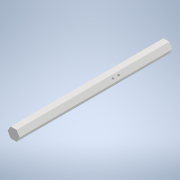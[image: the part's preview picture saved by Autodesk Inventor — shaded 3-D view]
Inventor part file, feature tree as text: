
AUTODESK INVENTOR PART (.ipt)
format: ipt  version: 2022 (Build 260153000, 153)  size: 117,248 bytes
history: native  units: mm
features: other x4, reference x3, extrude x2, sketch x2
ambient origin geometry x8: Origin, YZ Plane, XZ Plane, XY Plane, X Axis, Y Axis, Z Axis, Center Point
bodies: Solid1 (feature_tree)
feature tree (11):
  extrude  "Extrusion1"  Depth=3.1mm TaperAngle=360.0deg
  extrude  "Extrusion3"  Depth=80.0mm
  sketch  "Sketch1"  dims[d0=3.1mm d1=60.0mm d3=360.0deg]
  reference  "Reference1"
  reference  "Reference2"
  sketch  "Sketch2"  dims[d5=80.0mm d6=0.0mm d7=1.3mm d8=49.7mm d9=3.0mm d12=80.0mm d13=0.0mm]
  reference  "Reference3"
  other  "<userpath>\OneDrive\Escritorio\Mini_Proyecto_Diseno\Diseno_18012\Modelo_MPD\caja_nuevo.iam"
  other  "caja_nuevo.iam"
  other  "Rodamiento_Ejes:3"
  other  "hombro_nuevo:8"
